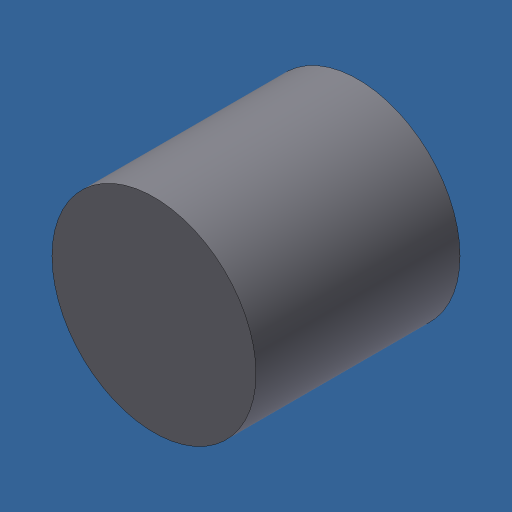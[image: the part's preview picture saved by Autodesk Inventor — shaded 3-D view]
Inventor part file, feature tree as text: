
AUTODESK INVENTOR PART (.ipt)
format: ipt  version: 2024.3 (Build 283343000, 343)  size: 128,000 bytes
history: native  units: mm (DEFAULTED — no unit token found)
features: other x1, extrude x1
ambient origin geometry x8: Origin, YZ Plane, XZ Plane, XY Plane, X Axis, Y Axis, Z Axis, Center Point
bodies: Body1 (feature_tree)
feature tree (2):
  other  "Finish - None"
  extrude  "Extrusion1"  TaperAngle=0.0deg  [1 undecoded]
note: 1 required parameter value undecoded (feature->parameter linkage not recoverable at this tier; creation-order binding heuristic only, values carry confidence <= 0.55)
